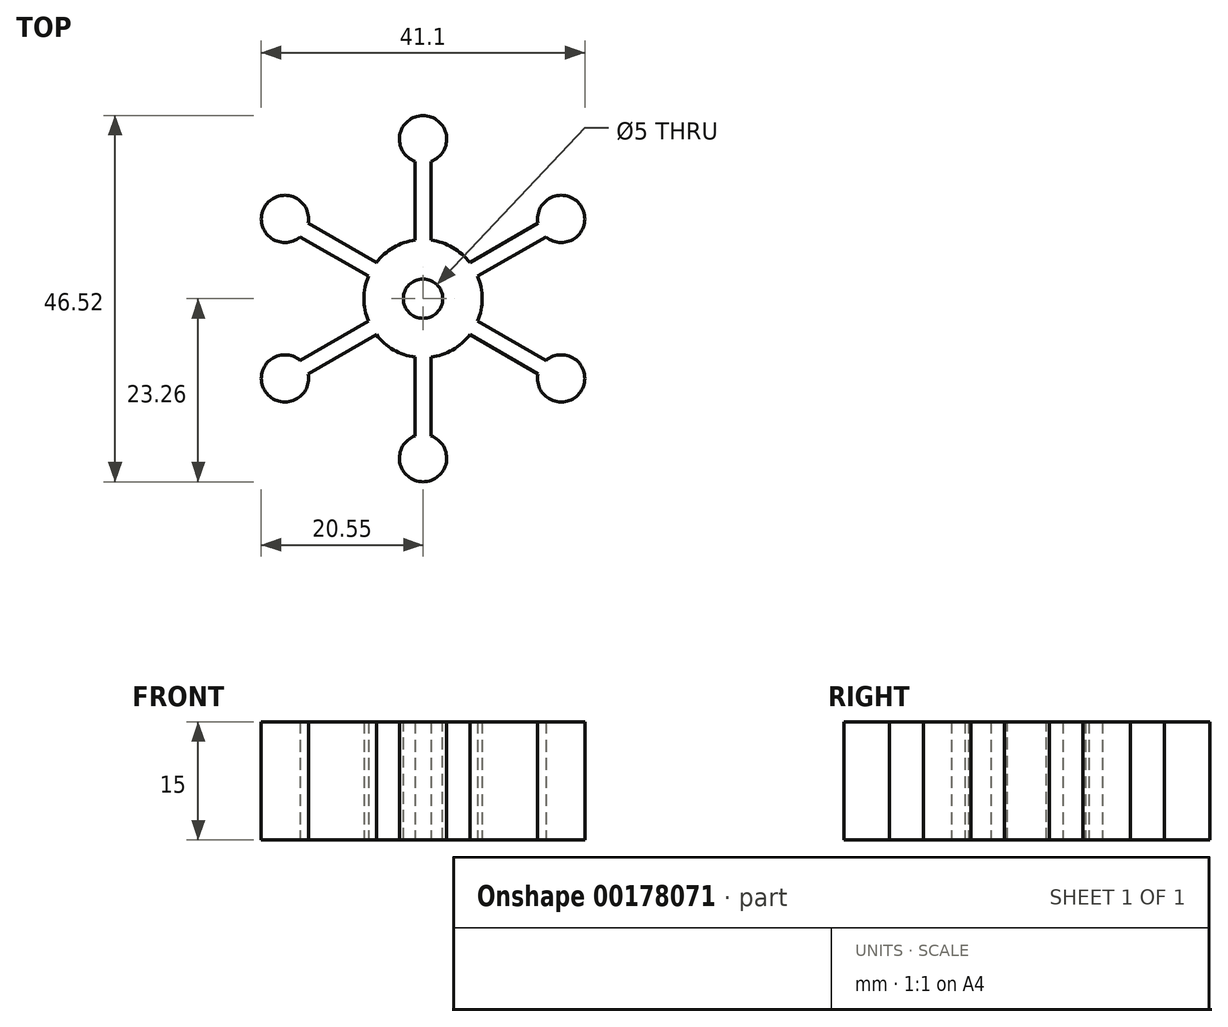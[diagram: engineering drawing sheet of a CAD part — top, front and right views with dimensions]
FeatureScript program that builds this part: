
annotation { "Feature Type Name" : "Feature", "Feature Type Description" : "" }
export const myFeature = defineFeature(function(context is Context, id is Id, definition is map)
    precondition{}
    {
        {
            var Q0;
            Q0=qCreatedBy(makeId("Top.planeOp"),FACE);
            var sketch = newSketch(context, id + "F0", { "sketchPlane" : qUnion([Q0])});
            skCircle(sketch, "E0", {"center": v(0, 0) * mm, "radius": 7.5 * mm});
            skLineSegment(sketch, "E1", {"start": v(0, 0) * mm, "end": v(0, 7.5) * mm, "construction": true});
            skCircle(sketch, "E2", {"center": v(0, 20.26) * mm, "radius": 3 * mm});
            skLineSegment(sketch, "E3", {"start": v(-1, 17.43) * mm, "end": v(-1, 7.43) * mm});
            skLineSegment(sketch, "E4.MirrorCS", {"start": v(1, 17.43) * mm, "end": v(1, 7.43) * mm});
            skCircle(sketch, "E5.1.0", {"center": v(-17.55, 10.13) * mm, "radius": 3 * mm});
            skLineSegment(sketch, "E5.1.1", {"start": v(-15.6, 7.85) * mm, "end": v(-6.94, 2.85) * mm});
            skLineSegment(sketch, "E5.1.2", {"start": v(-14.6, 9.58) * mm, "end": v(-5.94, 4.58) * mm});
            skCircle(sketch, "E5.2.0", {"center": v(-17.55, -10.13) * mm, "radius": 3 * mm});
            skLineSegment(sketch, "E5.2.1", {"start": v(-14.6, -9.58) * mm, "end": v(-5.94, -4.58) * mm});
            skLineSegment(sketch, "E5.2.2", {"start": v(-15.6, -7.85) * mm, "end": v(-6.94, -2.85) * mm});
            skCircle(sketch, "E6.1.3.0", {"center": v(0, -20.26) * mm, "radius": 3 * mm});
            skLineSegment(sketch, "E6.2.3.0", {"start": v(1, -17.43) * mm, "end": v(1, -7.43) * mm});
            skLineSegment(sketch, "E6.5.3.0", {"start": v(-1, -17.43) * mm, "end": v(-1, -7.43) * mm});
            skCircle(sketch, "E7.1.4.0", {"center": v(17.55, -10.13) * mm, "radius": 3 * mm});
            skLineSegment(sketch, "E7.2.4.0", {"start": v(15.6, -7.85) * mm, "end": v(6.94, -2.85) * mm});
            skLineSegment(sketch, "E7.5.4.0", {"start": v(14.6, -9.58) * mm, "end": v(5.94, -4.58) * mm});
            skCircle(sketch, "E7.1.5.0", {"center": v(17.55, 10.13) * mm, "radius": 3 * mm});
            skLineSegment(sketch, "E7.2.5.0", {"start": v(14.6, 9.58) * mm, "end": v(5.94, 4.58) * mm});
            skLineSegment(sketch, "E7.5.5.0", {"start": v(15.6, 7.85) * mm, "end": v(6.94, 2.85) * mm});
            skSolve(sketch);
        }
        {
            var Q0;
            Q0=qSketchRegion(id+"F0",true);
            extrude(context, id + "F1", {"entities" : qUnion([Q0]), "depth" : 15 * mm});
        }
        {
            var Q0;
            Q0=makeQuery(id+"F1.opExtrude","CAP_FACE",FACE,{"disambiguationData":[OSD([sQuery(id+"F0.wireOp",EDGE,"E0"),sQuery(id+"F0.wireOp",EDGE,"E2"),sQuery(id+"F0.wireOp",EDGE,"E3"),sQuery(id+"F0.wireOp",EDGE,"E4.MirrorCS"),sQuery(id+"F0.wireOp",EDGE,"E5.1.0"),sQuery(id+"F0.wireOp",EDGE,"E5.1.1"),sQuery(id+"F0.wireOp",EDGE,"E5.1.2"),sQuery(id+"F0.wireOp",EDGE,"E5.2.0"),sQuery(id+"F0.wireOp",EDGE,"E5.2.1"),sQuery(id+"F0.wireOp",EDGE,"E5.2.2"),sQuery(id+"F0.wireOp",EDGE,"E6.1.3.0"),sQuery(id+"F0.wireOp",EDGE,"E6.2.3.0"),sQuery(id+"F0.wireOp",EDGE,"E6.5.3.0"),sQuery(id+"F0.wireOp",EDGE,"E6.1.4.0"),sQuery(id+"F0.wireOp",EDGE,"E6.2.4.0"),sQuery(id+"F0.wireOp",EDGE,"E6.5.4.0"),sQuery(id+"F0.wireOp",EDGE,"E6.1.5.0"),sQuery(id+"F0.wireOp",EDGE,"E6.2.5.0"),sQuery(id+"F0.wireOp",EDGE,"E6.5.5.0"),sQuery(id+"F0.wireOp",EDGE,"E6.1.6.0"),sQuery(id+"F0.wireOp",EDGE,"E6.2.6.0"),sQuery(id+"F0.wireOp",EDGE,"E6.5.6.0"),sQuery(id+"F0.wireOp",EDGE,"E6.1.7.0"),sQuery(id+"F0.wireOp",EDGE,"E6.2.7.0"),sQuery(id+"F0.wireOp",EDGE,"E6.5.7.0"),sQuery(id+"F0.wireOp",EDGE,"E6.1.8.0"),sQuery(id+"F0.wireOp",EDGE,"E6.2.8.0"),sQuery(id+"F0.wireOp",EDGE,"E6.5.8.0"),sQuery(id+"F0.wireOp",EDGE,"E6.1.9.0"),sQuery(id+"F0.wireOp",EDGE,"E6.2.9.0"),sQuery(id+"F0.wireOp",EDGE,"E6.5.9.0")])],"isStart":false});
            var sketch = newSketch(context, id + "F2", { "sketchPlane" : qUnion([Q0])});
            skCircle(sketch, "E8", {"center": v(0, 0) * mm, "radius": 2.5 * mm});
            skSolve(sketch);
        }
        {
            var Q0;
            Q0=qSketchRegion(id+"F2",true);
            extrude(context, id + "F3", {"entities" : qUnion([Q0]), "operationType" : NewBodyOperationType.REMOVE, "endBound" : BoundingType.THROUGH_ALL, "oppositeDirection" : true, "depth" : 25 * mm});
        }
    });
